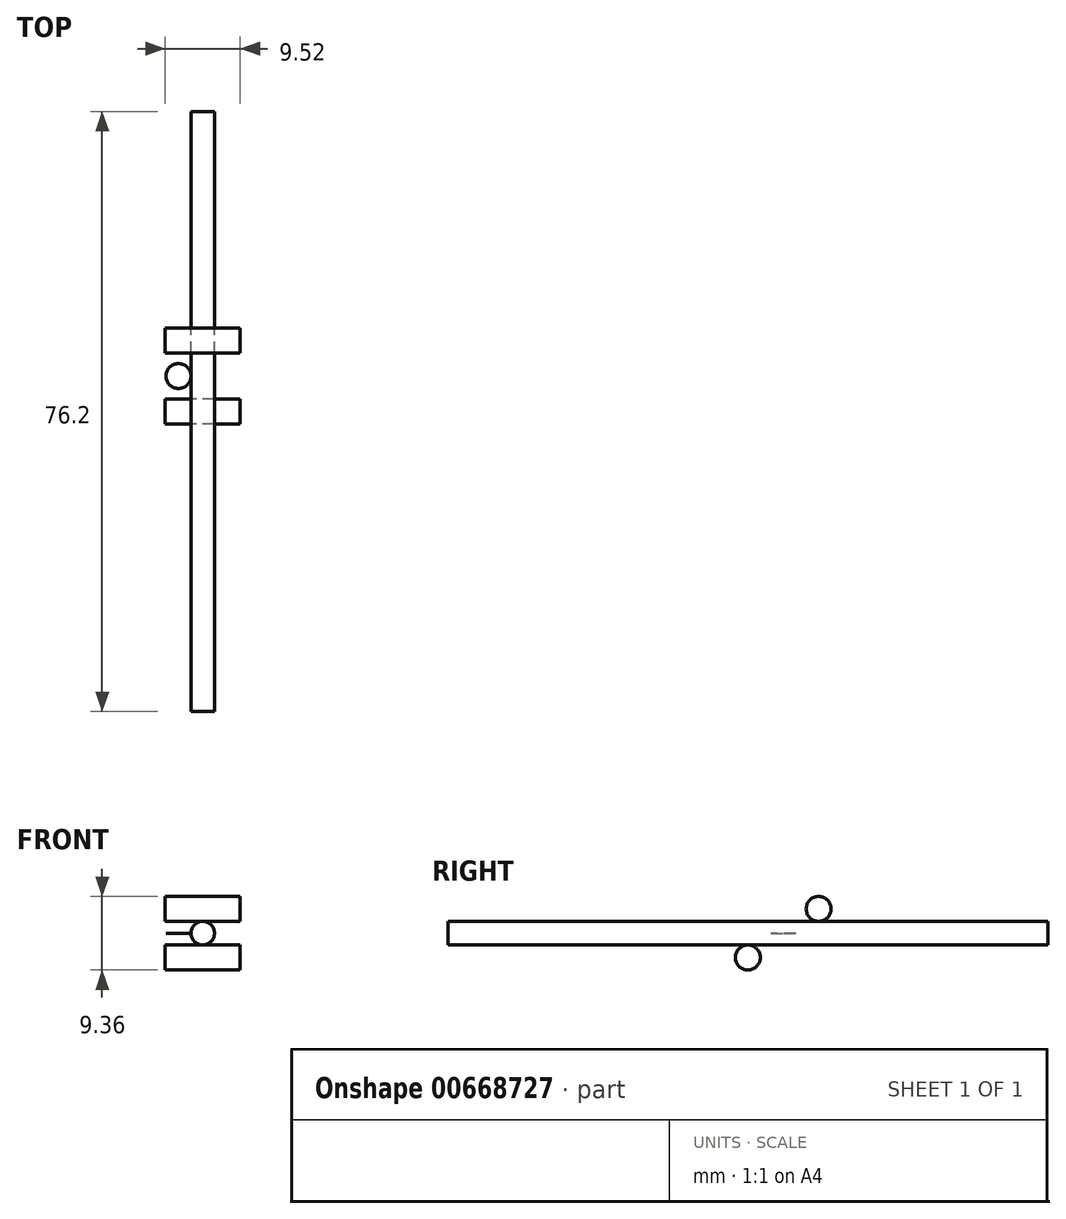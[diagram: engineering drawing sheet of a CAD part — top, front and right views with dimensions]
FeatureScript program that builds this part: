
annotation { "Feature Type Name" : "Feature", "Feature Type Description" : "" }
export const myFeature = defineFeature(function(context is Context, id is Id, definition is map)
    precondition{}
    {
        {
            var Q0;
            Q0=qCreatedBy(makeId("Front.planeOp"),FACE);
            var sketch = newSketch(context, id + "F0", { "sketchPlane" : qUnion([Q0])});
            skCircle(sketch, "E0", {"center": v(0, 0) * mm, "radius": 1.5 * mm});
            skLineSegment(sketch, "E1", {"start": v(-4.76, -3.09) * mm, "end": v(4.76, -3.09) * mm});
            skPoint(sketch, "E2", {"position": v(0, -3.09) * mm});
            skLineSegment(sketch, "E3.bottom", {"start": v(-4.76, -1.5) * mm, "end": v(4.76, -1.5) * mm});
            skLineSegment(sketch, "E3.top", {"start": v(-4.76, -4.67) * mm, "end": v(4.76, -4.67) * mm, "construction": true});
            skLineSegment(sketch, "E3.left", {"start": v(-4.76, -1.5) * mm, "end": v(-4.76, -3.09) * mm});
            skLineSegment(sketch, "E3.right", {"start": v(4.76, -1.5) * mm, "end": v(4.76, -3.09) * mm});
            skLineSegment(sketch, "E4", {"start": v(-4.76, -3.09) * mm, "end": v(-4.76, -4.67) * mm, "construction": true});
            skLineSegment(sketch, "E5", {"start": v(4.76, -3.09) * mm, "end": v(4.76, -4.67) * mm});
            skLineSegment(sketch, "E6", {"start": v(0, 0) * mm, "end": v(-6.04, 0) * mm, "construction": true});
            skLineSegment(sketch, "E7.MirrorCS", {"start": v(-4.76, 3.09) * mm, "end": v(4.76, 3.09) * mm});
            skLineSegment(sketch, "E8.MirrorCS", {"start": v(-4.76, 1.5) * mm, "end": v(-4.76, 3.09) * mm});
            skLineSegment(sketch, "E9.MirrorCS", {"start": v(4.76, 1.5) * mm, "end": v(4.76, 3.09) * mm});
            skLineSegment(sketch, "E10.MirrorCS", {"start": v(-4.76, 3.09) * mm, "end": v(-4.76, 4.67) * mm, "construction": true});
            skLineSegment(sketch, "E11.MirrorCS", {"start": v(4.76, 3.09) * mm, "end": v(4.76, 4.67) * mm});
            skPoint(sketch, "E12.MirrorP", {"position": v(0, 3.09) * mm});
            skLineSegment(sketch, "E13.MirrorCS", {"start": v(-4.76, 1.5) * mm, "end": v(4.76, 1.5) * mm});
            skSolve(sketch);
        }
        {
            var Q0;
            Q0=makeQuery(id+"F0.imprint","IMPRINT",FACE,{"disambiguationData":[TD([[makeQuery(id+"F0.imprint","IMPRINT",EDGE,{"derivedFrom":sQuery(id+"F0.wireOp",EDGE,"E0")}),1.0]])]});
            extrude(context, id + "F1", {"entities" : qUnion([Q0]), "depth" : 76.2 * mm, "offsetDistance" : 25 * mm, "symmetric" : true});
        }
        {
            var Q0;
            Q0=makeQuery(id+"F0.imprint","IMPRINT",FACE,{"disambiguationData":[TD([[makeQuery(id+"F0.imprint","IMPRINT",EDGE,{"derivedFrom":sQuery(id+"F0.wireOp",EDGE,"E1")}),1.0]])]});
            var Q1;
            Q1=sQuery(id+"F0.wireOp",EDGE,"E1");
            revolve(context, id + "F2", {"entities" : qUnion([Q0]), "axis" : qUnion([Q1]), "revolveType" : RevolveType.FULL});
        }
        {
            var Q0;
            Q0=qCreatedBy(makeId("Top.planeOp"),FACE);
            var sketch = newSketch(context, id + "F3", { "sketchPlane" : qUnion([Q0])});
            skCircle(sketch, "E14", {"center": v(-3.09, 4.5) * mm, "radius": 1.59 * mm});
            skLineSegment(sketch, "E15", {"start": v(-1.5, -12.5) * mm, "end": v(-1.5, 12.5) * mm, "construction": true});
            skLineSegment(sketch, "E16", {"start": v(1.5, 12.5) * mm, "end": v(1.5, -12.5) * mm, "construction": true});
            skLineSegment(sketch, "E17", {"start": v(0, 0) * mm, "end": v(0, 12.55) * mm, "construction": true});
            skCircle(sketch, "E18.MirrorC", {"center": v(3.09, 4.5) * mm, "radius": 1.59 * mm});
            skSolve(sketch);
        }
        {
            var Q0;
            Q0=makeQuery(id+"F3.imprint","IMPRINT",FACE,{"disambiguationData":[TD([[makeQuery(id+"F3.imprint","IMPRINT",EDGE,{"derivedFrom":sQuery(id+"F3.wireOp",EDGE,"E18.MirrorC")}),-1.0]])]});
            var Q1;
            Q1=makeQuery(id+"F3.imprint","IMPRINT",FACE,{"disambiguationData":[TD([[makeQuery(id+"F3.imprint","IMPRINT",EDGE,{"derivedFrom":sQuery(id+"F3.wireOp",EDGE,"E14")}),1.0]])]});
            extrude(context, id + "F4", {"entities" : qUnion([Q0, Q1]), "depth" : 3 / 203.2 * mm, "offsetDistance" : 25 * mm, "symmetric" : true});
        }
        {
            var Q0;
            Q0=makeQuery(id+"F0.imprint","IMPRINT",FACE,{"disambiguationData":[TD([[makeQuery(id+"F0.imprint","IMPRINT",EDGE,{"derivedFrom":sQuery(id+"F0.wireOp",EDGE,"E7.MirrorCS")}),-1.0]])]});
            var Q1;
            Q1=sQuery(id+"F0.wireOp",EDGE,"E7.MirrorCS");
            revolve(context, id + "F5", {"entities" : qUnion([Q0]), "axis" : qUnion([Q1]), "revolveType" : RevolveType.FULL});
        }
        {
            var Q0;
            Q0=makeQuery(id+"F5.opRevolve","SWEPT_BODY",BODY,{"disambiguationData":[OSD([sQuery(id+"F0.wireOp",EDGE,"E7.MirrorCS"),sQuery(id+"F0.wireOp",EDGE,"E8.MirrorCS"),sQuery(id+"F0.wireOp",EDGE,"E9.MirrorCS"),sQuery(id+"F0.wireOp",EDGE,"E13.MirrorCS")])]});
            var Q1;
            Q1=makeQuery(id+"F1.opExtrude","SWEPT_FACE",FACE,{"disambiguationData":[OSD([sQuery(id+"F0.wireOp",EDGE,"E0")])]});
            transform(context, id + "F6", {"entities" : qUnion([Q0]), "transformType" : TransformType.TRANSLATION_DISTANCE, "transformDirection" : qUnion([Q1]), "distance" : 9 * mm, "makeCopy" : false});
        }
    });
